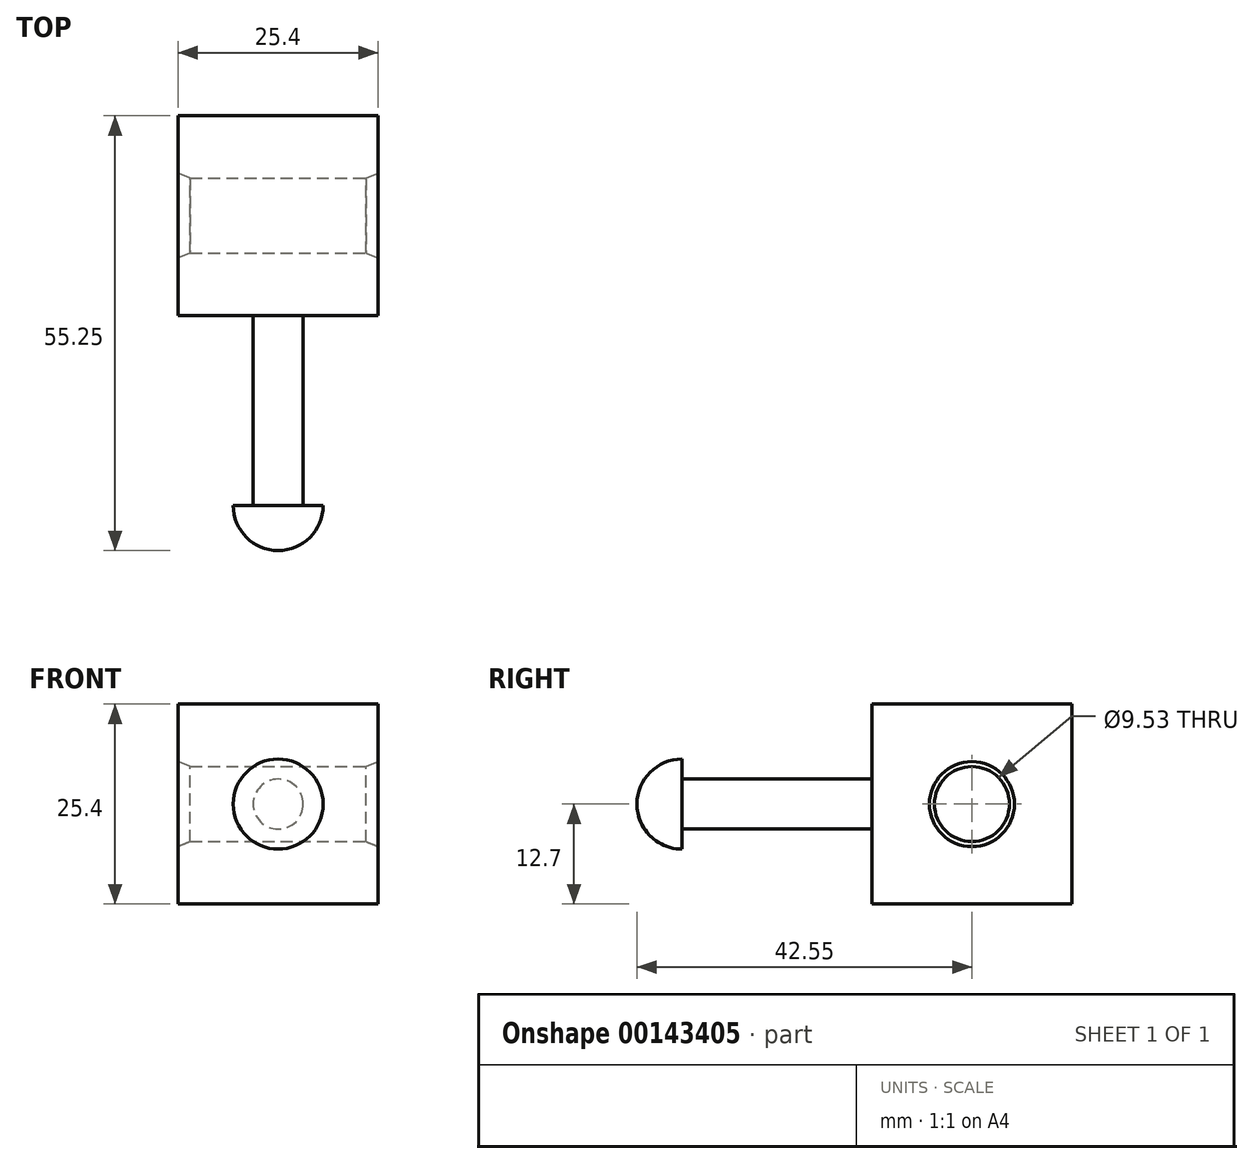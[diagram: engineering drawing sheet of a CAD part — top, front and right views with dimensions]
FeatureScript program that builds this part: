
annotation { "Feature Type Name" : "Feature", "Feature Type Description" : "" }
export const myFeature = defineFeature(function(context is Context, id is Id, definition is map)
    precondition{}
    {
        {
            var Q0;
            Q0=qCreatedBy(makeId("Right.planeOp"),FACE);
            var sketch = newSketch(context, id + "F0", { "sketchPlane" : qUnion([Q0])});
            skLineSegment(sketch, "E0.bottom", {"start": v(-12.7, 12.7) * mm, "end": v(12.7, 12.7) * mm});
            skLineSegment(sketch, "E0.top", {"start": v(-12.7, -12.7) * mm, "end": v(12.7, -12.7) * mm});
            skLineSegment(sketch, "E0.left", {"start": v(-12.7, 12.7) * mm, "end": v(-12.7, -12.7) * mm});
            skLineSegment(sketch, "E0.right", {"start": v(12.7, 12.7) * mm, "end": v(12.7, -12.7) * mm});
            skSolve(sketch);
        }
        {
            var Q0;
            Q0=makeQuery(id+"F0.imprint","IMPRINT",FACE,{"disambiguationData":[TD([[makeQuery(id+"F0.imprint","IMPRINT",EDGE,{"derivedFrom":sQuery(id+"F0.wireOp",EDGE,"E0.bottom")}),-1.0]])]});
            extrude(context, id + "F1", {"entities" : qUnion([Q0]), "oppositeDirection" : true, "depth" : 12.7 * mm});
        }
        {
            var Q0;
            Q0=makeQuery(id+"F1.opExtrude","CAP_FACE",FACE,{"disambiguationData":[OSD([sQuery(id+"F0.wireOp",EDGE,"E0.bottom"),sQuery(id+"F0.wireOp",EDGE,"E0.top"),sQuery(id+"F0.wireOp",EDGE,"E0.left"),sQuery(id+"F0.wireOp",EDGE,"E0.right")])],"isStart":true});
            var sketch = newSketch(context, id + "F2", { "sketchPlane" : qUnion([Q0])});
            skCircle(sketch, "E1", {"center": v(0, 0) * mm, "radius": 4.76 * mm});
            skSolve(sketch);
        }
        {
            var Q0;
            Q0=sQuery(id+"F2.wireOp",VERTEX,"E1.center");
            var Q1;
            Q1=makeQuery(id+"F1.opExtrude","SWEPT_BODY",BODY,{"disambiguationData":[OSD([sQuery(id+"F0.wireOp",EDGE,"E0.bottom"),sQuery(id+"F0.wireOp",EDGE,"E0.top"),sQuery(id+"F0.wireOp",EDGE,"E0.left"),sQuery(id+"F0.wireOp",EDGE,"E0.right")])]});
            hole(context, id + "F3", {"style" : HoleStyle.C_SINK, "endStyle" : HoleEndStyle.THROUGH, "holeDiameter" : 9.52 * mm, "cSinkDiameter" : 10.8 * mm, "cSinkAngle" : 45 * degree, "startFromSketch" : true, "locations" : qUnion([Q0]), "scope" : qUnion([Q1]), "isTappedThrough" : true});
        }
        {
            var Q0;
            Q0=makeQuery(id+"F1.opExtrude","SWEPT_BODY",BODY,{"disambiguationData":[OSD([sQuery(id+"F0.wireOp",EDGE,"E0.bottom"),sQuery(id+"F0.wireOp",EDGE,"E0.top"),sQuery(id+"F0.wireOp",EDGE,"E0.left"),sQuery(id+"F0.wireOp",EDGE,"E0.right")])]});
            var Q1;
            Q1=makeQuery(id+"F1.opExtrude","CAP_FACE",FACE,{"disambiguationData":[OSD([sQuery(id+"F0.wireOp",EDGE,"E0.bottom"),sQuery(id+"F0.wireOp",EDGE,"E0.top"),sQuery(id+"F0.wireOp",EDGE,"E0.left"),sQuery(id+"F0.wireOp",EDGE,"E0.right")])],"isStart":false});
            mirror(context, id + "F4", {"operationType" : NewBodyOperationType.ADD, "entities" : qUnion([Q0]), "mirrorPlane" : qUnion([Q1])});
        }
        {
            var Q0;
            {var subQ0=makeQuery(id+"F1.opExtrude","SWEPT_FACE",FACE,{"disambiguationData":[OSD([sQuery(id+"F0.wireOp",EDGE,"E0.left")])]});Q0=makeQuery(id+"F4.boolean.opBoolean","MERGE",FACE,{"derivedFrom":[subQ0,makeQuery(id+"F4.opPattern","COPY",FACE,{"derivedFrom":subQ0,"instanceName":"1"})]});}
            var sketch = newSketch(context, id + "F5", { "sketchPlane" : qUnion([Q0])});
            skLineSegment(sketch, "E2", {"start": v(-12.7, 12.7) * mm, "end": v(-12.7, -12.7) * mm, "construction": true});
            skLineSegment(sketch, "E3", {"start": v(-25.4, 0) * mm, "end": v(0, 0) * mm, "construction": true});
            skCircle(sketch, "E4", {"center": v(-12.7, 0) * mm, "radius": 3.18 * mm});
            skSolve(sketch);
        }
        {
            var Q0;
            Q0=makeQuery(id+"F5.imprint","IMPRINT",FACE,{"disambiguationData":[TD([[makeQuery(id+"F5.imprint","IMPRINT",EDGE,{"derivedFrom":sQuery(id+"F5.wireOp",EDGE,"E4")}),1.0]])]});
            extrude(context, id + "F6", {"entities" : qUnion([Q0]), "operationType" : NewBodyOperationType.ADD, "depth" : 24.13 * mm});
        }
        {
            var Q0;
            Q0=makeQuery(id+"F4.opPattern","COPY",FACE,{"derivedFrom":makeQuery(id+"F1.opExtrude","CAP_FACE",FACE,{"disambiguationData":[OSD([sQuery(id+"F0.wireOp",EDGE,"E0.bottom"),sQuery(id+"F0.wireOp",EDGE,"E0.top"),sQuery(id+"F0.wireOp",EDGE,"E0.left"),sQuery(id+"F0.wireOp",EDGE,"E0.right")])],"isStart":true}),"instanceName":"1"});
            cPlane(context, id + "F7", {"entities" : qUnion([Q0]), "cplaneType" : CPlaneType.OFFSET, "offset" : 12.7 * mm, "oppositeDirection" : true, "width" : 152.4 * mm, "height" : 152.4 * mm});
        }
        {
            var Q0;
            Q0=qCreatedBy(id+"F7.planeOp",FACE);
            var sketch = newSketch(context, id + "F8", { "sketchPlane" : qUnion([Q0])});
            skLineSegment(sketch, "E5.0", {"start": v(36.83, 3.18) * mm, "end": v(36.83, -3.17) * mm});
            skLineSegment(sketch, "E6", {"start": v(36.83, 0) * mm, "end": v(36.83, 5.72) * mm});
            skArc(sketch, "E7", {"start": v(42.55, 0) * mm, "mid": v(40.87, 4.04) * mm, "end": v(36.83, 5.72) * mm});
            skLineSegment(sketch, "E8", {"start": v(42.55, 0) * mm, "end": v(36.83, 0) * mm});
            skSolve(sketch);
        }
        {
            var Q0;
            {var subQ2=sQuery(id+"F8.wireOp",EDGE,"E7");Q0=makeQuery(id+"F8.imprint","IMPRINT",FACE,{"disambiguationData":[TD([[makeQuery(id+"F8.imprint","IMPRINT",EDGE,{"derivedFrom":subQ2}),1.0]])]});}
            var Q1;
            Q1=sQuery(id+"F8.wireOp",EDGE,"E8");
            revolve(context, id + "F9", {"operationType" : NewBodyOperationType.ADD, "entities" : qUnion([Q0]), "axis" : qUnion([Q1]), "revolveType" : RevolveType.FULL});
        }
    });
